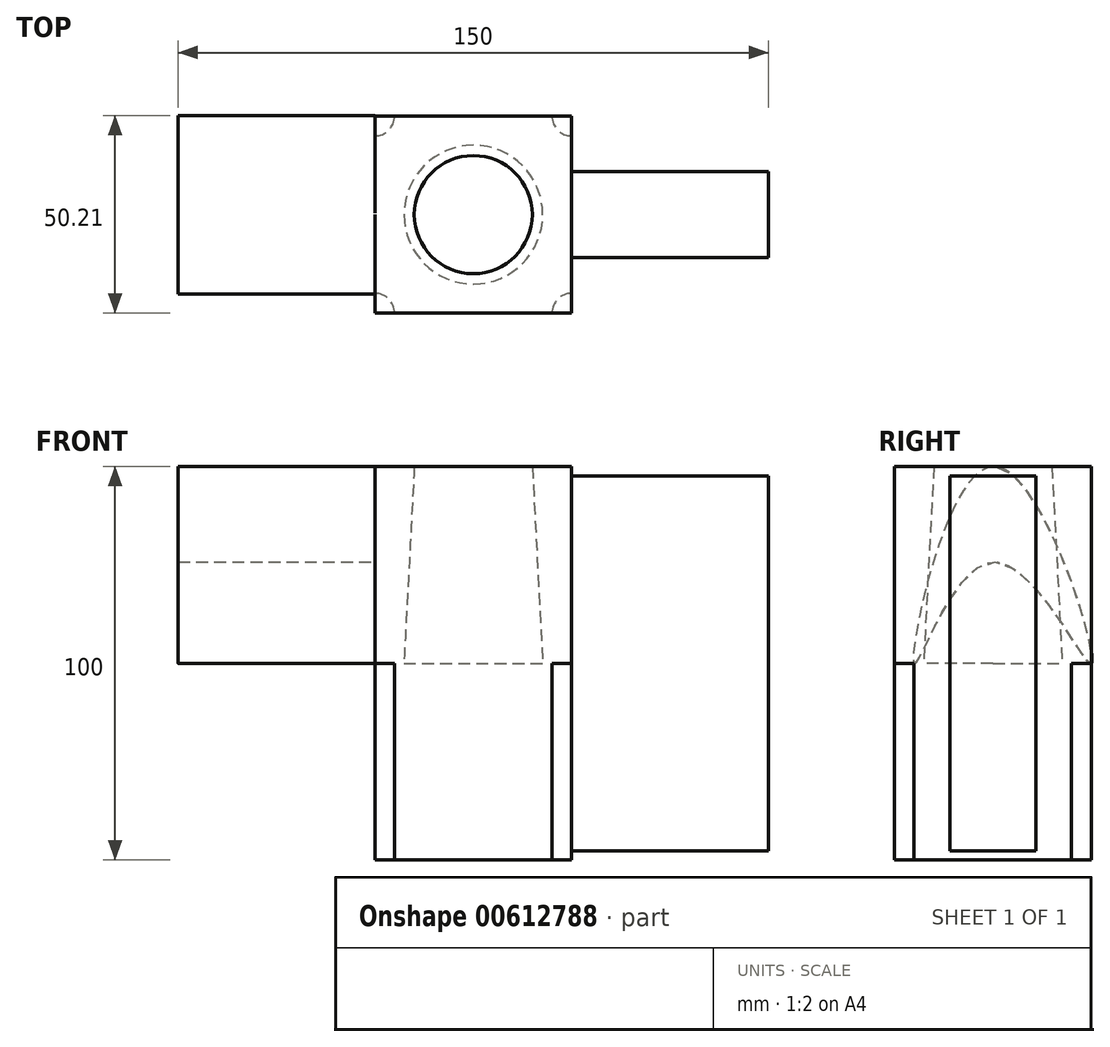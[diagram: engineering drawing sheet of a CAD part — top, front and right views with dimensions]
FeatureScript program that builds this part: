
annotation { "Feature Type Name" : "Feature", "Feature Type Description" : "" }
export const myFeature = defineFeature(function(context is Context, id is Id, definition is map)
    precondition{}
    {
        {
            var Q0;
            Q0=qCreatedBy(makeId("Top.planeOp"),FACE);
            var sketch = newSketch(context, id + "F0", { "sketchPlane" : qUnion([Q0])});
            skLineSegment(sketch, "E0.bottom", {"start": v(-25, 25) * mm, "end": v(25, 25) * mm});
            skLineSegment(sketch, "E0.top", {"start": v(-25, -25) * mm, "end": v(25, -25) * mm});
            skLineSegment(sketch, "E0.left", {"start": v(-25, 25) * mm, "end": v(-25, -25) * mm});
            skLineSegment(sketch, "E0.right", {"start": v(25, 25) * mm, "end": v(25, -25) * mm});
            skPoint(sketch, "E0.middle", {"position": v(0, 0) * mm});
            skSolve(sketch);
        }
        {
            var Q0;
            Q0 = qSketchRegion(id + "F0", true);
            extrude(context, id + "F1", {"entities" : qUnion([Q0]), "depth" : 50 * mm, "offsetDistance" : 25 * mm});
        }
        {
            var Q0;
            Q0=makeQuery(id+"F1.opExtrude","CAP_FACE",FACE,{"disambiguationData":[OSD([sQuery(id+"F0.wireOp",EDGE,"E0.bottom"),sQuery(id+"F0.wireOp",EDGE,"E0.top"),sQuery(id+"F0.wireOp",EDGE,"E0.left"),sQuery(id+"F0.wireOp",EDGE,"E0.right")])],"isStart":false});
            var sketch = newSketch(context, id + "F2", { "sketchPlane" : qUnion([Q0])});
            skCircle(sketch, "E1", {"center": v(0, 0) * mm, "radius": 15 * mm});
            skSolve(sketch);
        }
        {
            var Q0;
            Q0 = qSketchRegion(id + "F2", true);
            extrude(context, id + "F3", {"entities" : qUnion([Q0]), "operationType" : NewBodyOperationType.REMOVE, "oppositeDirection" : true, "depth" : 50 * mm, "offsetDistance" : 25 * mm, "hasDraft" : true, "draftAngle" : 3 * degree, "hasSecondDirection" : true, "secondDirectionOppositeDirection" : false, "secondDirectionDepth" : 25 * mm});
        }
        {
            var Q0;
            Q0=qCreatedBy(makeId("Top.planeOp"),FACE);
            var sketch = newSketch(context, id + "F4", { "sketchPlane" : qUnion([Q0])});
            skLineSegment(sketch, "E2.bottom", {"start": v(25, -25) * mm, "end": v(-25, -25) * mm});
            skLineSegment(sketch, "E2.top", {"start": v(25, 25) * mm, "end": v(-25, 25) * mm});
            skLineSegment(sketch, "E2.left", {"start": v(25, -25) * mm, "end": v(25, 25) * mm});
            skLineSegment(sketch, "E2.right", {"start": v(-25, -25) * mm, "end": v(-25, 25) * mm});
            skPoint(sketch, "E2.middle", {"position": v(0, 0) * mm});
            skCircle(sketch, "E3", {"center": v(-25, -25) * mm, "radius": 5 * mm});
            skCircle(sketch, "E4", {"center": v(-25, 25) * mm, "radius": 5 * mm});
            skCircle(sketch, "E5", {"center": v(25, 25) * mm, "radius": 5 * mm});
            skCircle(sketch, "E6", {"center": v(25, -25) * mm, "radius": 5 * mm});
            skSolve(sketch);
        }
        {
            var Q0;
            {var subQ5=sQuery(id+"F4.wireOp",EDGE,"E6");var subQ10=sQuery(id+"F4.wireOp",EDGE,"E2.bottom");var subQ11=makeQuery(id+"F4.imprint","INTERSECT",VERTEX,{"derivedFrom":[subQ10,subQ5]});Q0=makeQuery(id+"F4.imprint","IMPRINT",FACE,{"disambiguationData":[TD([[makeQuery(id+"F4.imprint","IMPRINT",EDGE,{"disambiguationData":[TD([[subQ11,-1.0]])],"derivedFrom":subQ10}),-1.0]])]});}
            extrude(context, id + "F5", {"entities" : qUnion([Q0]), "operationType" : NewBodyOperationType.ADD, "oppositeDirection" : true, "depth" : 50 * mm, "offsetDistance" : 25 * mm});
        }
        {
            var Q0;
            Q0=makeQuery(id+"F5.boolean.opBoolean","MERGE",FACE,{"derivedFrom":[makeQuery(id+"F1.opExtrude","SWEPT_FACE",FACE,{"disambiguationData":[OSD([sQuery(id+"F0.wireOp",EDGE,"E0.left")])]}),makeQuery(id+"F5.opExtrude","SWEPT_FACE",FACE,{"disambiguationData":[OSD([sQuery(id+"F4.wireOp",EDGE,"E2.right")])]})]});
            var sketch = newSketch(context, id + "F6", { "sketchPlane" : qUnion([Q0])});
            skFitSpline(sketch, "E7", {"points": [v(20, 0) * mm, v(0, 25.73) * mm, v(-25, 0) * mm, v(0, 50) * mm, v(20, 0) * mm]});
            skSolve(sketch);
        }
        {
            var Q0;
            {var subQ0=sQuery(id+"F6.wireOp",EDGE,"E7");var subQ1=sQuery(id+"F0.wireOp",EDGE,"E0.left");var subQ2=sQuery(id+"F0.wireOp",EDGE,"E0.bottom");var subQ3=makeQuery(id+"F5.boolean.opBoolean","SPLIT",EDGE,{"disambiguationData":[TD([makeQuery(id+"F1.opExtrude","SWEPT_FACE",FACE,{"disambiguationData":[OSD([subQ2])]})])],"derivedFrom":makeQuery(id+"F1.opExtrude","CAP_EDGE",EDGE,{"disambiguationData":[OSD([subQ1])],"isStart":true})});var subQ5=makeQuery(id+"F6.imprint","INTERSECT",VERTEX,{"derivedFrom":[subQ3,subQ0]});Q0=makeQuery(id+"F6.imprint","IMPRINT",FACE,{"disambiguationData":[TD([[makeQuery(id+"F6.imprint","IMPRINT",EDGE,{"disambiguationData":[TD([[subQ5,-1.0]])],"derivedFrom":subQ0}),-1.0]])]});}
            var Q1;
            {var subQ0=sQuery(id+"F6.wireOp",EDGE,"E7");var subQ1=sQuery(id+"F0.wireOp",EDGE,"E0.left");var subQ2=sQuery(id+"F0.wireOp",EDGE,"E0.bottom");var subQ3=makeQuery(id+"F1.opExtrude","SWEPT_EDGE",EDGE,{"disambiguationData":[OSD([subQ2,subQ1])]});var subQ5=makeQuery(id+"F6.imprint","INTERSECT",VERTEX,{"derivedFrom":[subQ3,subQ0]});Q1=makeQuery(id+"F6.imprint","IMPRINT",FACE,{"disambiguationData":[TD([[makeQuery(id+"F6.imprint","IMPRINT",EDGE,{"disambiguationData":[TD([[subQ5,1.0]])],"derivedFrom":subQ0}),-1.0]])]});}
            var Q2;
            {var subQ0=sQuery(id+"F6.wireOp",EDGE,"E7");var subQ1=makeQuery(id+"F1.opExtrude","CAP_EDGE",EDGE,{"disambiguationData":[OSD([sQuery(id+"F0.wireOp",EDGE,"E0.left")])],"isStart":false});var subQ2=makeQuery(id+"F6.imprint","INTERSECT",VERTEX,{"disambiguationData":[OD(0.0)],"derivedFrom":[subQ1,subQ0]});Q2=makeQuery(id+"F6.imprint","IMPRINT",FACE,{"disambiguationData":[TD([[makeQuery(id+"F6.imprint","IMPRINT",EDGE,{"disambiguationData":[TD([[subQ2,-1.0]])],"derivedFrom":subQ0}),-1.0]])]});}
            var Q3;
            {var subQ0=sQuery(id+"F6.wireOp",EDGE,"E7");var subQ1=sQuery(id+"F0.wireOp",EDGE,"E0.left");var subQ13=makeQuery(id+"F1.opExtrude","CAP_EDGE",EDGE,{"disambiguationData":[OSD([subQ1])],"isStart":false});var subQ14=makeQuery(id+"F6.imprint","INTERSECT",VERTEX,{"disambiguationData":[OD(0.0)],"derivedFrom":[subQ13,subQ0]});Q3=makeQuery(id+"F6.imprint","IMPRINT",FACE,{"disambiguationData":[TD([[makeQuery(id+"F6.imprint","IMPRINT",EDGE,{"disambiguationData":[TD([[subQ14,-1.0]])],"derivedFrom":subQ13}),-1.0]])]});}
            extrude(context, id + "F7", {"entities" : qUnion([Q0, Q1, Q2, Q3]), "operationType" : NewBodyOperationType.ADD, "depth" : 50 * mm, "offsetDistance" : 25 * mm});
        }
        {
            var Q0;
            Q0=makeQuery(id+"F5.boolean.opBoolean","MERGE",FACE,{"derivedFrom":[makeQuery(id+"F1.opExtrude","SWEPT_FACE",FACE,{"disambiguationData":[OSD([sQuery(id+"F0.wireOp",EDGE,"E0.right")])]}),makeQuery(id+"F5.opExtrude","SWEPT_FACE",FACE,{"disambiguationData":[OSD([sQuery(id+"F4.wireOp",EDGE,"E2.left")])]})]});
            var sketch = newSketch(context, id + "F8", { "sketchPlane" : qUnion([Q0])});
            skLineSegment(sketch, "E8.bottom", {"start": v(-10.94, 47.6) * mm, "end": v(10.94, 47.6) * mm});
            skLineSegment(sketch, "E8.top", {"start": v(-10.94, -47.6) * mm, "end": v(10.94, -47.6) * mm});
            skLineSegment(sketch, "E8.left", {"start": v(-10.94, 47.6) * mm, "end": v(-10.94, -47.6) * mm});
            skLineSegment(sketch, "E8.right", {"start": v(10.94, 47.6) * mm, "end": v(10.94, -47.6) * mm});
            skPoint(sketch, "E8.middle", {"position": v(0, 0) * mm});
            skSolve(sketch);
        }
        {
            var Q0;
            Q0=makeQuery(id+"F8.imprint","IMPRINT",FACE,{"disambiguationData":[TD([[makeQuery(id+"F8.imprint","IMPRINT",EDGE,{"derivedFrom":sQuery(id+"F8.wireOp",EDGE,"E8.bottom")}),-1.0]])]});
            extrude(context, id + "F9", {"entities" : qUnion([Q0]), "operationType" : NewBodyOperationType.ADD, "depth" : 50 * mm, "offsetDistance" : 25 * mm});
        }
    });
